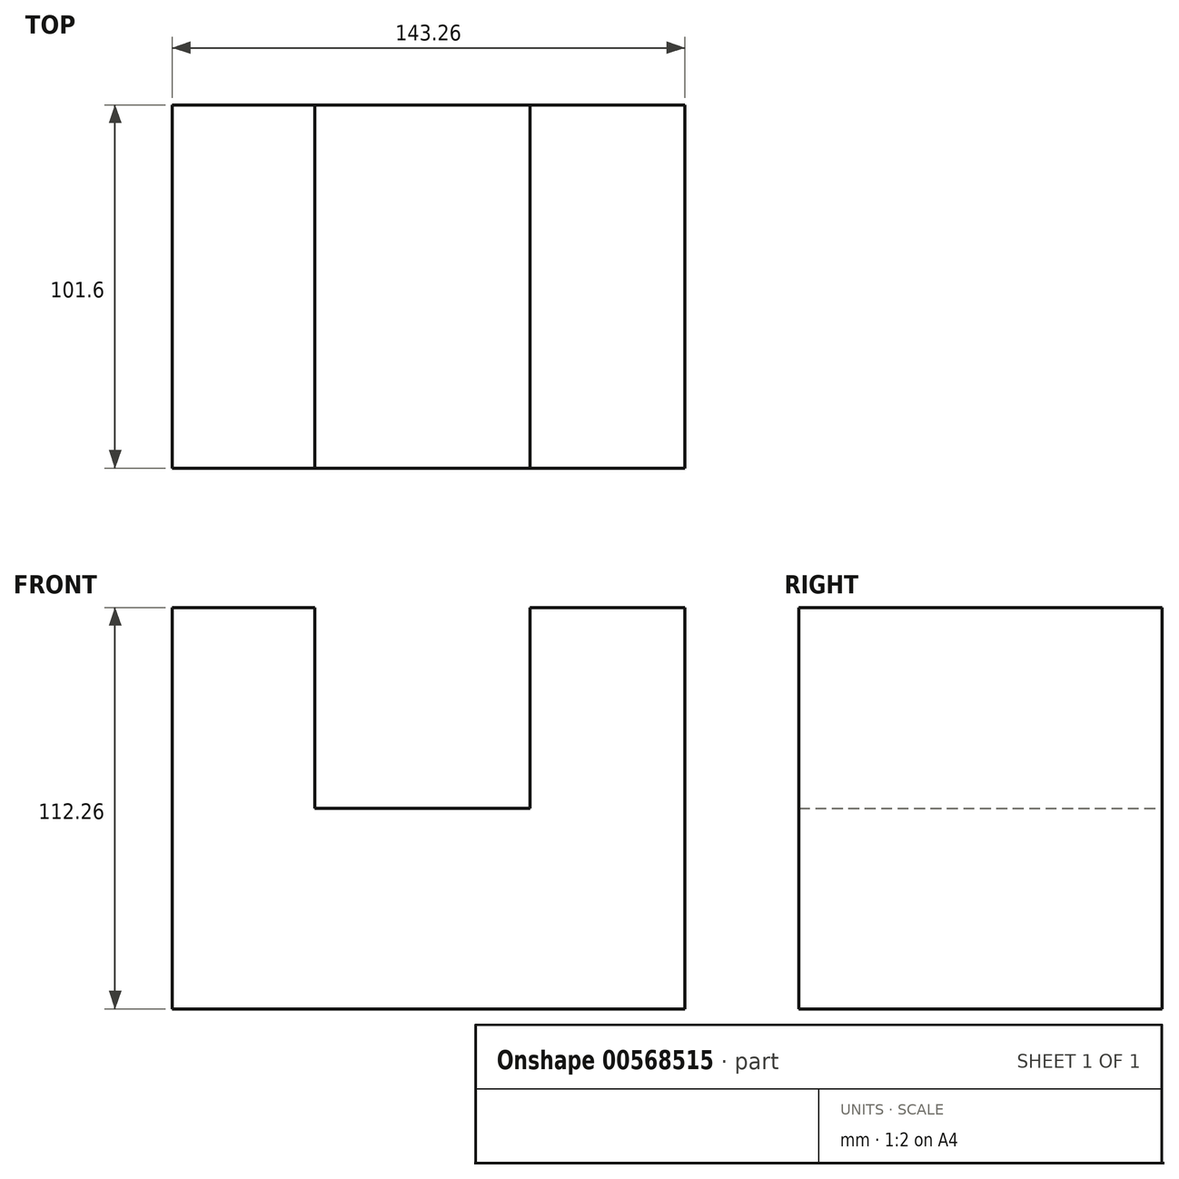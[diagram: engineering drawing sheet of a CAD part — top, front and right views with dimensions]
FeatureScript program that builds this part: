
annotation { "Feature Type Name" : "Feature", "Feature Type Description" : "" }
export const myFeature = defineFeature(function(context is Context, id is Id, definition is map)
    precondition{}
    {
        {
            var Q0;
            Q0=qCreatedBy(makeId("Front.planeOp"),FACE);
            var sketch = newSketch(context, id + "F0", { "sketchPlane" : qUnion([Q0])});
            skLineSegment(sketch, "E0", {"start": v(0, 0) * mm, "end": v(0, 56.13) * mm});
            skLineSegment(sketch, "E1", {"start": v(0, 56.13) * mm, "end": v(43.18, 56.13) * mm});
            skLineSegment(sketch, "E2", {"start": v(43.18, 56.13) * mm, "end": v(43.18, -56.13) * mm});
            skLineSegment(sketch, "E3", {"start": v(43.18, -56.13) * mm, "end": v(-100.08, -56.13) * mm});
            skLineSegment(sketch, "E4", {"start": v(-100.08, -56.13) * mm, "end": v(-100.08, 56.13) * mm});
            skLineSegment(sketch, "E5", {"start": v(-100.08, 56.13) * mm, "end": v(-60.2, 56.13) * mm});
            skLineSegment(sketch, "E6", {"start": v(-60.2, 56.13) * mm, "end": v(-60.2, 0) * mm});
            skLineSegment(sketch, "E7", {"start": v(-60.2, 0) * mm, "end": v(0, 0) * mm});
            skSolve(sketch);
        }
        {
            var Q0;
            Q0 = qSketchRegion(id + "F0", true);
            extrude(context, id + "F1", {"entities" : qUnion([Q0]), "depth" : 101.6 * mm, "offsetDistance" : 25.4 * mm});
        }
    });
